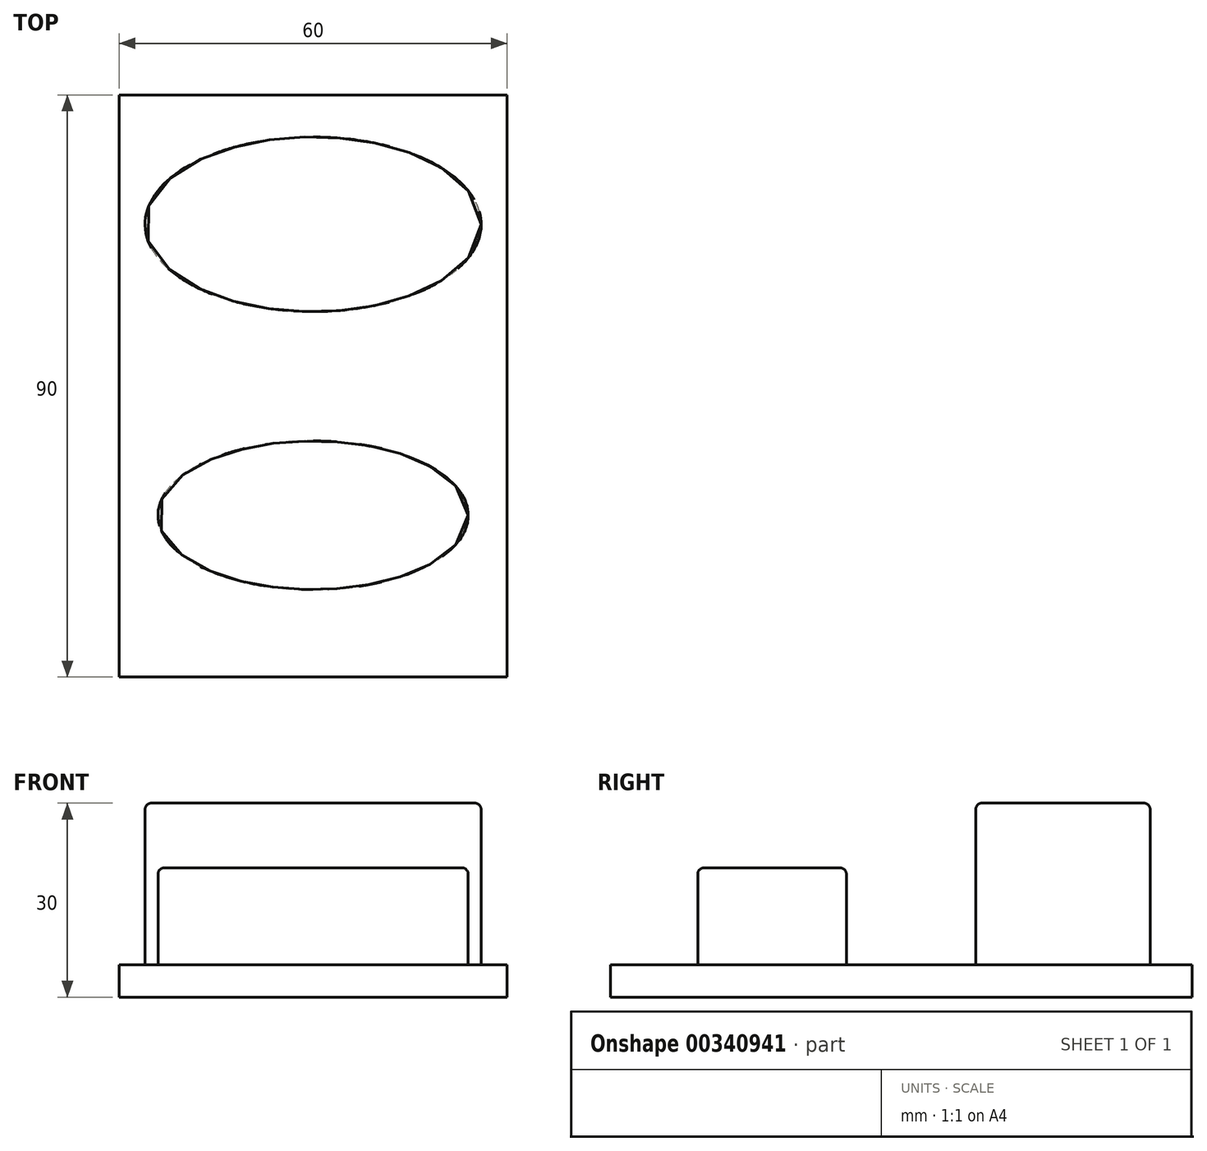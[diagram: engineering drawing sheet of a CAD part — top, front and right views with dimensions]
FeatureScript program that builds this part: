
annotation { "Feature Type Name" : "Feature", "Feature Type Description" : "" }
export const myFeature = defineFeature(function(context is Context, id is Id, definition is map)
    precondition{}
    {
        {
            var Q0;
            Q0=qCreatedBy(makeId("Top.planeOp"),FACE);
            var sketch = newSketch(context, id + "F0", { "sketchPlane" : qUnion([Q0])});
            skEllipse(sketch, "E0", {"center": v(0, 0) * mm, "majorRadius": 24 * mm, "minorRadius": 11.5 * mm, "majorAxis": v(1, 0)});
            skSolve(sketch);
        }
        {
            var Q0;
            Q0 = qSketchRegion(id + "F0", true);
            extrude(context, id + "F1", {"entities" : qUnion([Q0]), "depth" : 15 * mm});
        }
        {
            var Q0;
            Q0=qCreatedBy(makeId("Top.planeOp"),FACE);
            var sketch = newSketch(context, id + "F2", { "sketchPlane" : qUnion([Q0])});
            skLineSegment(sketch, "E1", {"start": v(0, 0) * mm, "end": v(0, 45) * mm, "construction": true});
            skEllipse(sketch, "E2", {"center": v(0, 45) * mm, "majorRadius": 26 * mm, "minorRadius": 13.5 * mm, "majorAxis": v(1, 0)});
            skSolve(sketch);
        }
        {
            var Q0;
            Q0 = qSketchRegion(id + "F2", true);
            extrude(context, id + "F3", {"entities" : qUnion([Q0]), "operationType" : NewBodyOperationType.ADD, "depth" : 25 * mm});
        }
        {
            var Q0;
            Q0=makeQuery(id+"F1.opExtrude","CAP_EDGE",EDGE,{"disambiguationData":[OSD([sQuery(id+"F0.wireOp",EDGE,"E0")])],"isStart":false});
            var Q1;
            Q1=makeQuery(id+"F3.opExtrude","CAP_EDGE",EDGE,{"disambiguationData":[OSD([sQuery(id+"F2.wireOp",EDGE,"E2")])],"isStart":false});
            fillet(context, id + "F4", {"entities" : qUnion([Q0, Q1]), "radius" : 1 * mm, "tangentPropagation" : true, "allowEdgeOverflow" : false});
        }
        {
            var Q0;
            Q0=qCreatedBy(makeId("Top.planeOp"),FACE);
            var sketch = newSketch(context, id + "F5", { "sketchPlane" : qUnion([Q0])});
            skLineSegment(sketch, "E3", {"start": v(0, 0) * mm, "end": v(0, -25) * mm, "construction": true});
            skLineSegment(sketch, "E4", {"start": v(0, -25) * mm, "end": v(30, -25) * mm, "construction": true});
            skLineSegment(sketch, "E5.bottom", {"start": v(30, -25) * mm, "end": v(-30, -25) * mm});
            skLineSegment(sketch, "E5.top", {"start": v(30, 65) * mm, "end": v(-30, 65) * mm});
            skLineSegment(sketch, "E5.left", {"start": v(30, -25) * mm, "end": v(30, 65) * mm});
            skLineSegment(sketch, "E5.right", {"start": v(-30, -25) * mm, "end": v(-30, 65) * mm});
            skSolve(sketch);
        }
        {
            var Q0;
            Q0 = qSketchRegion(id + "F5", true);
            extrude(context, id + "F6", {"entities" : qUnion([Q0]), "operationType" : NewBodyOperationType.ADD, "oppositeDirection" : true, "depth" : 5 * mm});
        }
    });
